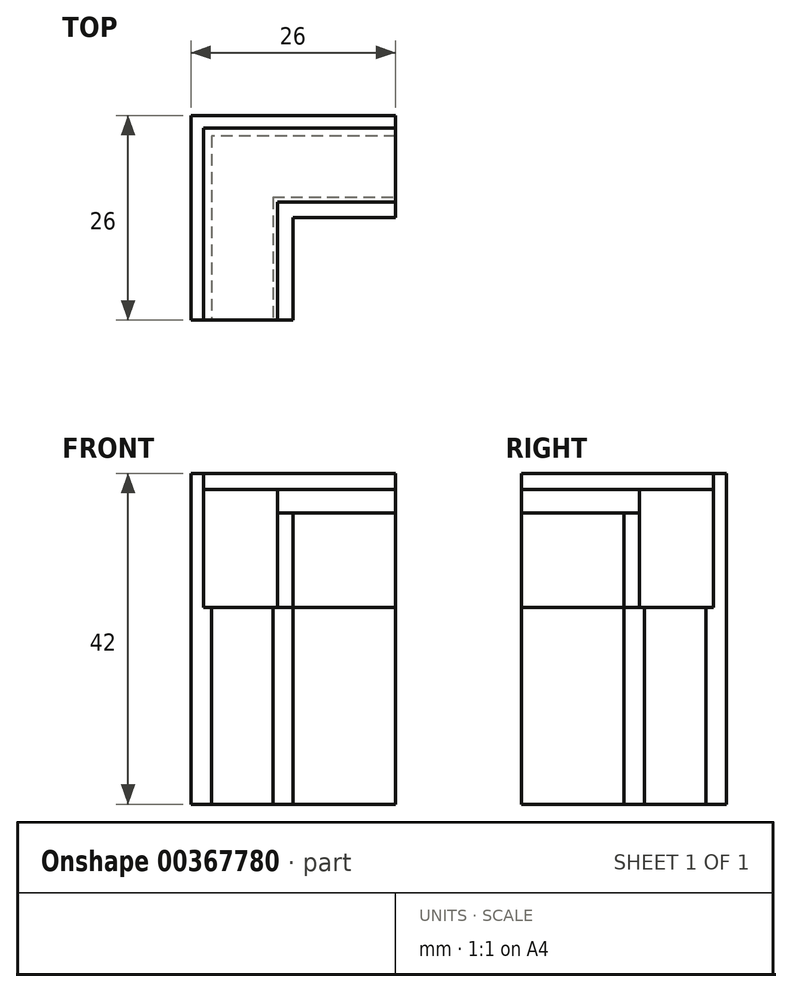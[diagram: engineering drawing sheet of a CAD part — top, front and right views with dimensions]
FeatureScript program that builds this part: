
annotation { "Feature Type Name" : "Feature", "Feature Type Description" : "" }
export const myFeature = defineFeature(function(context is Context, id is Id, definition is map)
    precondition{}
    {
        {
            var Q0;
            Q0=qCreatedBy(makeId("Top.planeOp"),FACE);
            var sketch = newSketch(context, id + "F0", { "sketchPlane" : qUnion([Q0])});
            skLineSegment(sketch, "E0.top", {"start": v(0, -13) * mm, "end": v(-13, -13) * mm});
            skLineSegment(sketch, "E0.left", {"start": v(0, 0) * mm, "end": v(0, -13) * mm});
            skLineSegment(sketch, "E0.right", {"start": v(-13, 0) * mm, "end": v(-13, -13) * mm});
            skLineSegment(sketch, "E1.bottom", {"start": v(0, 0) * mm, "end": v(13, 0) * mm});
            skLineSegment(sketch, "E1.top", {"start": v(0, 13) * mm, "end": v(13, 13) * mm});
            skLineSegment(sketch, "E1.right", {"start": v(13, 0) * mm, "end": v(13, 13) * mm});
            skLineSegment(sketch, "E2.top", {"start": v(0, 13) * mm, "end": v(-13, 13) * mm});
            skLineSegment(sketch, "E2.right", {"start": v(-13, 0) * mm, "end": v(-13, 13) * mm});
            skLineSegment(sketch, "E3.0", {"start": v(-2, 2) * mm, "end": v(-2, -13) * mm});
            skLineSegment(sketch, "E3.1", {"start": v(-2, 2) * mm, "end": v(13, 2) * mm});
            skLineSegment(sketch, "E4.0", {"start": v(-11.4, 0) * mm, "end": v(-11.4, -13) * mm});
            skLineSegment(sketch, "E4.1", {"start": v(-11.4, 0) * mm, "end": v(-11.4, 11.4) * mm});
            skLineSegment(sketch, "E4.2", {"start": v(0, 11.4) * mm, "end": v(-11.4, 11.4) * mm});
            skLineSegment(sketch, "E4.3", {"start": v(0, 11.4) * mm, "end": v(13, 11.4) * mm});
            skLineSegment(sketch, "E5.0", {"start": v(-10.4, 0) * mm, "end": v(-10.4, -13) * mm});
            skLineSegment(sketch, "E5.1", {"start": v(-10.4, 0) * mm, "end": v(-10.4, 10.4) * mm});
            skLineSegment(sketch, "E5.2", {"start": v(0, 10.4) * mm, "end": v(-10.4, 10.4) * mm});
            skLineSegment(sketch, "E5.3", {"start": v(0, 10.4) * mm, "end": v(13, 10.4) * mm});
            skLineSegment(sketch, "E6.0", {"start": v(-2.6, 2.6) * mm, "end": v(-2.6, -13) * mm});
            skLineSegment(sketch, "E6.1", {"start": v(-2.6, 2.6) * mm, "end": v(13, 2.6) * mm});
            skSolve(sketch);
        }
        {
            var Q0;
            {var subQ3=sQuery(id+"F0.wireOp",EDGE,"E4.0");Q0=makeQuery(id+"F0.imprint","IMPRINT",FACE,{"disambiguationData":[TD([[makeQuery(id+"F0.imprint","IMPRINT",EDGE,{"derivedFrom":subQ3}),1.0]])]});}
            var Q1;
            {var subQ3=sQuery(id+"F0.wireOp",EDGE,"E0.right");Q1=makeQuery(id+"F0.imprint","IMPRINT",FACE,{"disambiguationData":[TD([[makeQuery(id+"F0.imprint","IMPRINT",EDGE,{"derivedFrom":subQ3}),1.0]])]});}
            var Q2;
            {var subQ3=sQuery(id+"F0.wireOp",EDGE,"E3.0");Q2=makeQuery(id+"F0.imprint","IMPRINT",FACE,{"disambiguationData":[TD([[makeQuery(id+"F0.imprint","IMPRINT",EDGE,{"derivedFrom":subQ3}),-1.0]])]});}
            var Q3;
            {var subQ3=sQuery(id+"F0.wireOp",EDGE,"E0.left");Q3=makeQuery(id+"F0.imprint","IMPRINT",FACE,{"disambiguationData":[TD([[makeQuery(id+"F0.imprint","IMPRINT",EDGE,{"derivedFrom":subQ3}),-1.0]])]});}
            extrude(context, id + "F1", {"entities" : qUnion([Q0, Q1, Q2, Q3]), "depth" : -25 * mm});
        }
        {
            var Q0;
            {var subQ3=sQuery(id+"F0.wireOp",EDGE,"E0.right");Q0=makeQuery(id+"F0.imprint","IMPRINT",FACE,{"disambiguationData":[TD([[makeQuery(id+"F0.imprint","IMPRINT",EDGE,{"derivedFrom":subQ3}),1.0]])]});}
            extrude(context, id + "F2", {"entities" : qUnion([Q0]), "operationType" : NewBodyOperationType.ADD, "depth" : 17 * mm});
        }
        {
            var Q0;
            {var subQ3=sQuery(id+"F0.wireOp",EDGE,"E4.0");Q0=makeQuery(id+"F0.imprint","IMPRINT",FACE,{"disambiguationData":[TD([[makeQuery(id+"F0.imprint","IMPRINT",EDGE,{"derivedFrom":subQ3}),1.0]])]});}
            var Q1;
            {var subQ3=sQuery(id+"F0.wireOp",EDGE,"E5.0");Q1=makeQuery(id+"F0.imprint","IMPRINT",FACE,{"disambiguationData":[TD([[makeQuery(id+"F0.imprint","IMPRINT",EDGE,{"derivedFrom":subQ3}),1.0]])]});}
            var Q2;
            {var subQ3=sQuery(id+"F0.wireOp",EDGE,"E3.0");Q2=makeQuery(id+"F0.imprint","IMPRINT",FACE,{"disambiguationData":[TD([[makeQuery(id+"F0.imprint","IMPRINT",EDGE,{"derivedFrom":subQ3}),-1.0]])]});}
            extrude(context, id + "F3", {"entities" : qUnion([Q0, Q1, Q2]), "depth" : 15 * mm});
        }
        {
            var Q0;
            {var subQ3=sQuery(id+"F0.wireOp",EDGE,"E0.left");Q0=makeQuery(id+"F0.imprint","IMPRINT",FACE,{"disambiguationData":[TD([[makeQuery(id+"F0.imprint","IMPRINT",EDGE,{"derivedFrom":subQ3}),-1.0]])]});}
            extrude(context, id + "F4", {"entities" : qUnion([Q0]), "depth" : 12 * mm});
        }
    });
